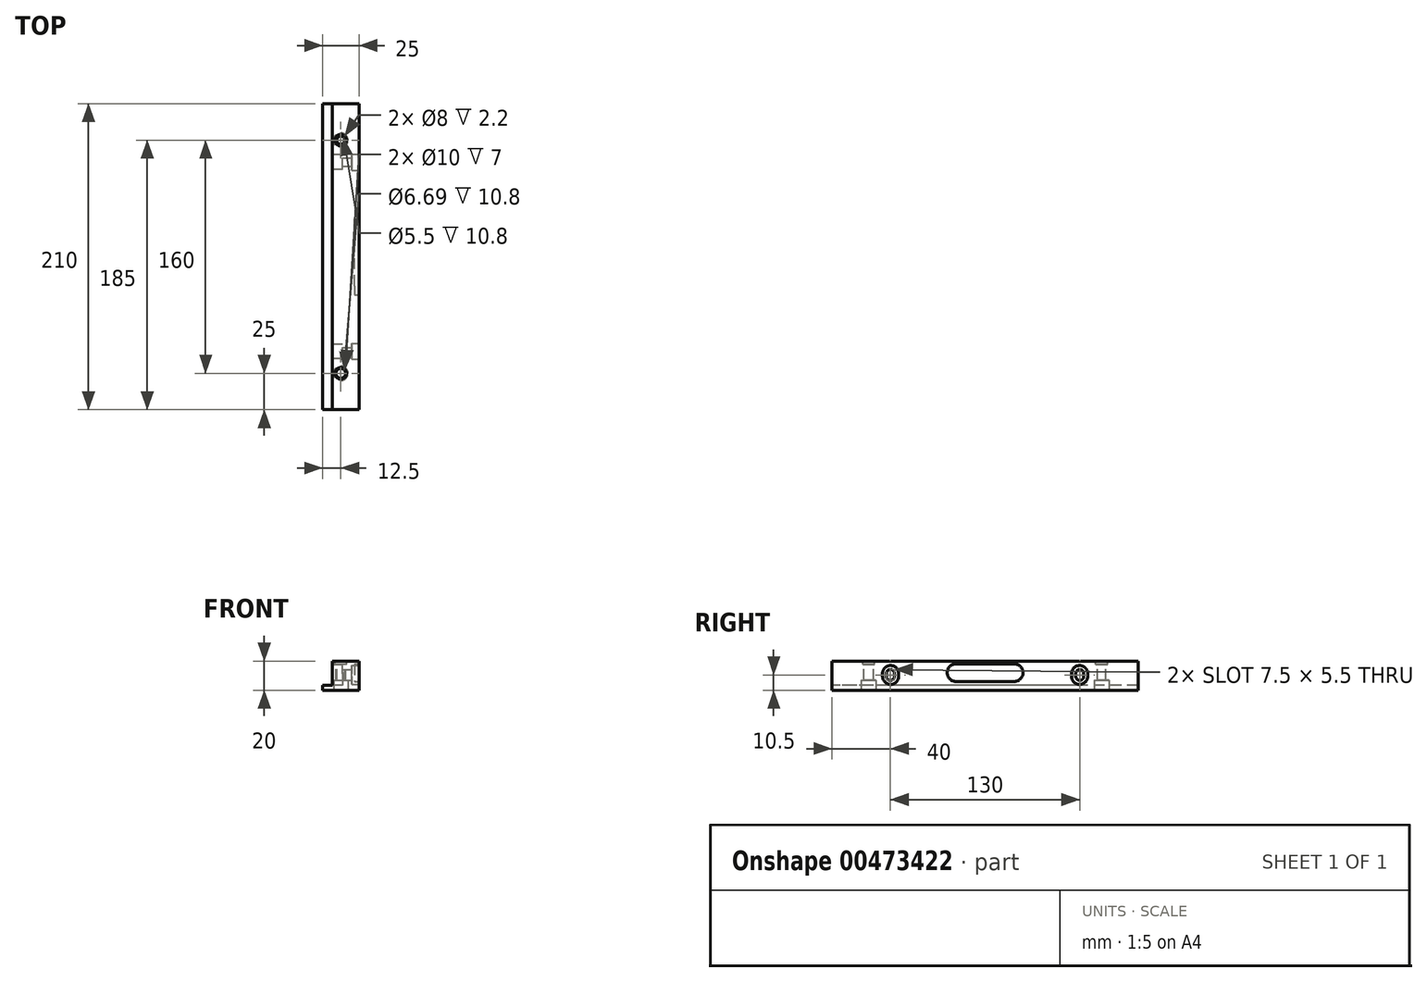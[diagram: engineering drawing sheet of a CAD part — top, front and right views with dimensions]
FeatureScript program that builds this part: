
annotation { "Feature Type Name" : "Feature", "Feature Type Description" : "" }
export const myFeature = defineFeature(function(context is Context, id is Id, definition is map)
    precondition{}
    {
        {
            var Q0;
            Q0=qCreatedBy(makeId("Front.planeOp"),FACE);
            var sketch = newSketch(context, id + "F0", { "sketchPlane" : qUnion([Q0])});
            skLineSegment(sketch, "E0", {"start": v(-12.5, -10) * mm, "end": v(12.5, -10) * mm});
            skLineSegment(sketch, "E1", {"start": v(12.5, 10) * mm, "end": v(-5.7, 10) * mm});
            skLineSegment(sketch, "E2", {"start": v(-5.7, 10) * mm, "end": v(-5.7, -6.5) * mm});
            skLineSegment(sketch, "E3", {"start": v(-5.7, -6.5) * mm, "end": v(-12.5, -6.5) * mm});
            skLineSegment(sketch, "E4", {"start": v(-12.5, -6.5) * mm, "end": v(-12.5, -10) * mm});
            skLineSegment(sketch, "E5", {"start": v(12.5, 10) * mm, "end": v(12.5, -10) * mm});
            skSolve(sketch);
        }
        {
            var Q0;
            Q0 = qSketchRegion(id + "F0", true);
            extrude(context, id + "F1", {"entities" : qUnion([Q0]), "endBound" : BoundingType.SYMMETRIC, "oppositeDirection" : true, "depth" : 210 * mm});
        }
        {
            var Q0;
            Q0=makeQuery(id+"F1.opExtrude","SWEPT_FACE",FACE,{"disambiguationData":[OSD([sQuery(id+"F0.wireOp",EDGE,"E1")])]});
            var sketch = newSketch(context, id + "F2", { "sketchPlane" : qUnion([Q0])});
            skCircle(sketch, "E6", {"center": v(0, 80) * mm, "radius": 2.75 * mm});
            skCircle(sketch, "E7", {"center": v(0, -80) * mm, "radius": 3.34 * mm});
            skSolve(sketch);
        }
        {
            var Q0;
            Q0 = qSketchRegion(id + "F2", true);
            extrude(context, id + "F3", {"entities" : qUnion([Q0]), "operationType" : NewBodyOperationType.REMOVE, "endBound" : BoundingType.THROUGH_ALL, "oppositeDirection" : true, "depth" : 25 * mm});
        }
        {
            var Q0;
            Q0=makeQuery(id+"F1.opExtrude","SWEPT_FACE",FACE,{"disambiguationData":[OSD([sQuery(id+"F0.wireOp",EDGE,"E5")])]});
            var sketch = newSketch(context, id + "F4", { "sketchPlane" : qUnion([Q0])});
            skLineSegment(sketch, "E8.bottom", {"start": v(-65, 4.25) * mm, "end": v(-65, 4.25) * mm});
            skLineSegment(sketch, "E8.top", {"start": v(-65, -3.25) * mm, "end": v(-65, -3.25) * mm});
            skLineSegment(sketch, "E8.left", {"start": v(-67.75, 1.5) * mm, "end": v(-67.75, -0.5) * mm});
            skLineSegment(sketch, "E8.right", {"start": v(-62.25, 1.5) * mm, "end": v(-62.25, -0.5) * mm});
            skLineSegment(sketch, "E9", {"start": v(0, 18.17) * mm, "end": v(0, -22.43) * mm, "construction": true});
            skPoint(sketch, "E9.endSnap0", {"position": v(0, -10) * mm});
            skPoint(sketch, "E10.visualSharp", {"position": v(-67.75, 4.25) * mm});
            skArc(sketch, "E10.filletArc", {"start": v(-65, 4.25) * mm, "mid": v(-66.94, 3.44) * mm, "end": v(-67.75, 1.5) * mm});
            skPoint(sketch, "E11.visualSharp", {"position": v(-62.25, -3.25) * mm});
            skArc(sketch, "E11.filletArc", {"start": v(-65, -3.25) * mm, "mid": v(-63.06, -2.44) * mm, "end": v(-62.25, -0.5) * mm});
            skPoint(sketch, "E12.visualSharp", {"position": v(-62.25, 4.25) * mm});
            skArc(sketch, "E12.filletArc", {"start": v(-62.25, 1.5) * mm, "mid": v(-63.06, 3.44) * mm, "end": v(-65, 4.25) * mm});
            skPoint(sketch, "E13.visualSharp", {"position": v(-67.75, -3.25) * mm});
            skArc(sketch, "E13.filletArc", {"start": v(-67.75, -0.5) * mm, "mid": v(-66.94, -2.44) * mm, "end": v(-65, -3.25) * mm});
            skLineSegment(sketch, "E14.MirrorCS", {"start": v(62.25, 1.5) * mm, "end": v(62.25, -0.5) * mm});
            skLineSegment(sketch, "E15.MirrorCS", {"start": v(67.75, 1.5) * mm, "end": v(67.75, -0.5) * mm});
            skPoint(sketch, "E16.MirrorP", {"position": v(62.25, -3.25) * mm});
            skArc(sketch, "E17.MirrorCS", {"start": v(65, 4.25) * mm, "mid": v(66.94, 3.44) * mm, "end": v(67.75, 1.5) * mm});
            skPoint(sketch, "E18.MirrorP", {"position": v(67.75, -3.25) * mm});
            skPoint(sketch, "E19.MirrorP", {"position": v(62.25, 4.25) * mm});
            skLineSegment(sketch, "E20.MirrorCS", {"start": v(65, 4.25) * mm, "end": v(65, 4.25) * mm});
            skArc(sketch, "E21.MirrorCS", {"start": v(62.25, 1.5) * mm, "mid": v(63.06, 3.44) * mm, "end": v(65, 4.25) * mm});
            skPoint(sketch, "E22.MirrorP", {"position": v(67.75, 4.25) * mm});
            skArc(sketch, "E23.MirrorCS", {"start": v(67.75, -0.5) * mm, "mid": v(66.94, -2.44) * mm, "end": v(65, -3.25) * mm});
            skLineSegment(sketch, "E24.MirrorCS", {"start": v(65, -3.25) * mm, "end": v(65, -3.25) * mm});
            skArc(sketch, "E25.MirrorCS", {"start": v(65, -3.25) * mm, "mid": v(63.06, -2.44) * mm, "end": v(62.25, -0.5) * mm});
            skSolve(sketch);
        }
        {
            var Q0;
            Q0 = qSketchRegion(id + "F4", true);
            extrude(context, id + "F5", {"entities" : qUnion([Q0]), "operationType" : NewBodyOperationType.REMOVE, "endBound" : BoundingType.THROUGH_ALL, "oppositeDirection" : true, "depth" : 25 * mm});
        }
        {
            var Q0;
            Q0=makeQuery(id+"F1.opExtrude","SWEPT_FACE",FACE,{"disambiguationData":[OSD([sQuery(id+"F0.wireOp",EDGE,"E5")])]});
            var sketch = newSketch(context, id + "F6", { "sketchPlane" : qUnion([Q0])});
            skLineSegment(sketch, "E26.bottom", {"start": v(-64.83, -6) * mm, "end": v(-64.86, -6) * mm});
            skLineSegment(sketch, "E26.top", {"start": v(-64.88, 7) * mm, "end": v(-64.9, 7) * mm});
            skLineSegment(sketch, "E26.left", {"start": v(-59.34, -0.38) * mm, "end": v(-59.38, 1.62) * mm});
            skLineSegment(sketch, "E26.right", {"start": v(-70.36, -0.62) * mm, "end": v(-70.5, 5.7) * mm});
            skPoint(sketch, "E26.middle", {"position": v(-64.87, 0.5) * mm});
            skPoint(sketch, "E26.cornerSnap0", {"position": v(-65, -3.25) * mm});
            skPoint(sketch, "E27.visualSharp", {"position": v(-70.24, -6) * mm});
            skArc(sketch, "E27.filletArc", {"start": v(-70.36, -0.62) * mm, "mid": v(-68.7, -4.43) * mm, "end": v(-64.86, -6) * mm});
            skLineSegment(sketch, "E28", {"start": v(-70.4, 1.38) * mm, "end": v(-70.5, 5.7) * mm});
            skPoint(sketch, "E29.visualSharp", {"position": v(-70.53, 7) * mm});
            skArc(sketch, "E29.filletArc", {"start": v(-64.9, 7) * mm, "mid": v(-68.84, 5.35) * mm, "end": v(-70.4, 1.38) * mm});
            skPoint(sketch, "E30.visualSharp", {"position": v(-59.5, 7) * mm});
            skArc(sketch, "E30.filletArc", {"start": v(-59.38, 1.62) * mm, "mid": v(-61.03, 5.43) * mm, "end": v(-64.88, 7) * mm});
            skPoint(sketch, "E31.visualSharp", {"position": v(-59.21, -6) * mm});
            skArc(sketch, "E31.filletArc", {"start": v(-64.83, -6) * mm, "mid": v(-60.9, -4.35) * mm, "end": v(-59.34, -0.38) * mm});
            skLineSegment(sketch, "E32", {"start": v(0, 18.83) * mm, "end": v(0, -21.12) * mm, "construction": true});
            skPoint(sketch, "E32.startSnap0", {"position": v(0, 10) * mm});
            skPoint(sketch, "E32.endSnap0", {"position": v(0, -10) * mm});
            skLineSegment(sketch, "E33.MirrorCS", {"start": v(59.34, -0.38) * mm, "end": v(59.38, 1.62) * mm});
            skLineSegment(sketch, "E34.MirrorCS", {"start": v(70.4, 1.38) * mm, "end": v(70.5, 5.7) * mm});
            skLineSegment(sketch, "E35.MirrorCS", {"start": v(64.83, -6) * mm, "end": v(64.86, -6) * mm});
            skArc(sketch, "E36.MirrorCS", {"start": v(64.83, -6) * mm, "mid": v(60.9, -4.35) * mm, "end": v(59.34, -0.38) * mm});
            skPoint(sketch, "E37.MirrorP", {"position": v(64.87, 0.5) * mm});
            skLineSegment(sketch, "E38.MirrorCS", {"start": v(64.88, 7) * mm, "end": v(64.9, 7) * mm});
            skPoint(sketch, "E39.MirrorP", {"position": v(59.5, 7) * mm});
            skArc(sketch, "E40.MirrorCS", {"start": v(70.36, -0.62) * mm, "mid": v(68.7, -4.43) * mm, "end": v(64.86, -6) * mm});
            skPoint(sketch, "E41.MirrorP", {"position": v(70.53, 7) * mm});
            skPoint(sketch, "E42.MirrorP", {"position": v(59.21, -6) * mm});
            skPoint(sketch, "E43.MirrorP", {"position": v(70.24, -6) * mm});
            skArc(sketch, "E44.MirrorCS", {"start": v(64.9, 7) * mm, "mid": v(68.84, 5.35) * mm, "end": v(70.4, 1.38) * mm});
            skLineSegment(sketch, "E45.MirrorCS", {"start": v(70.36, -0.62) * mm, "end": v(70.5, 5.7) * mm});
            skPoint(sketch, "E46.MirrorP", {"position": v(65, -3.25) * mm});
            skArc(sketch, "E47.MirrorCS", {"start": v(59.38, 1.62) * mm, "mid": v(61.03, 5.43) * mm, "end": v(64.88, 7) * mm});
            skSolve(sketch);
        }
        {
            var Q0;
            Q0 = qSketchRegion(id + "F6", true);
            extrude(context, id + "F7", {"entities" : qUnion([Q0]), "operationType" : NewBodyOperationType.REMOVE, "oppositeDirection" : true, "depth" : 5 * mm});
        }
        {
            var Q0;
            Q0=makeQuery(id+"F1.opExtrude","SWEPT_FACE",FACE,{"disambiguationData":[OSD([sQuery(id+"F0.wireOp",EDGE,"E2")])]});
            var sketch = newSketch(context, id + "F8", { "sketchPlane" : qUnion([Q0])});
            skLineSegment(sketch, "E48", {"start": v(0, 16.2) * mm, "end": v(0, -17.52) * mm, "construction": true});
            skPoint(sketch, "E48.endSnap0", {"position": v(0, 10) * mm});
            skLineSegment(sketch, "E49.bottom", {"start": v(-62.95, 6.83) * mm, "end": v(-62.95, 6.83) * mm});
            skLineSegment(sketch, "E49.top", {"start": v(-65, -6.5) * mm, "end": v(-65, -6.5) * mm});
            skLineSegment(sketch, "E49.left", {"start": v(-70, 2.27) * mm, "end": v(-70, -1.5) * mm});
            skLineSegment(sketch, "E49.right", {"start": v(-60, 2.27) * mm, "end": v(-60, -1.5) * mm});
            skPoint(sketch, "E50.visualSharp", {"position": v(-70, 10) * mm});
            skArc(sketch, "E50.filletArc", {"start": v(-62.95, 6.83) * mm, "mid": v(-67.71, 6.47) * mm, "end": v(-70, 2.27) * mm});
            skPoint(sketch, "E51.visualSharp", {"position": v(-60, 5.5) * mm});
            skArc(sketch, "E51.filletArc", {"start": v(-60, 2.27) * mm, "mid": v(-60.8, 4.98) * mm, "end": v(-62.95, 6.83) * mm});
            skPoint(sketch, "E52.visualSharp", {"position": v(-70, -6.5) * mm});
            skArc(sketch, "E52.filletArc", {"start": v(-70, -1.5) * mm, "mid": v(-68.54, -5.04) * mm, "end": v(-65, -6.5) * mm});
            skPoint(sketch, "E53.visualSharp", {"position": v(-60, -6.5) * mm});
            skArc(sketch, "E53.filletArc", {"start": v(-65, -6.5) * mm, "mid": v(-61.46, -5.04) * mm, "end": v(-60, -1.5) * mm});
            skLineSegment(sketch, "E54.MirrorCS", {"start": v(70, 2.27) * mm, "end": v(70, -1.5) * mm});
            skLineSegment(sketch, "E55.MirrorCS", {"start": v(60, 2.27) * mm, "end": v(60, -1.5) * mm});
            skArc(sketch, "E56.MirrorCS", {"start": v(60, 2.27) * mm, "mid": v(60.8, 4.98) * mm, "end": v(62.95, 6.83) * mm});
            skArc(sketch, "E57.MirrorCS", {"start": v(62.95, 6.83) * mm, "mid": v(67.71, 6.47) * mm, "end": v(70, 2.27) * mm});
            skArc(sketch, "E58.MirrorCS", {"start": v(65, -6.5) * mm, "mid": v(61.46, -5.04) * mm, "end": v(60, -1.5) * mm});
            skArc(sketch, "E59.MirrorCS", {"start": v(70, -1.5) * mm, "mid": v(68.54, -5.04) * mm, "end": v(65, -6.5) * mm});
            skPoint(sketch, "E60.MirrorP", {"position": v(60, -6.5) * mm});
            skLineSegment(sketch, "E61.MirrorCS", {"start": v(62.95, 6.83) * mm, "end": v(62.95, 6.83) * mm});
            skPoint(sketch, "E62.MirrorP", {"position": v(70, 10) * mm});
            skPoint(sketch, "E63.MirrorP", {"position": v(60, 5.5) * mm});
            skPoint(sketch, "E64.MirrorP", {"position": v(70, -6.5) * mm});
            skLineSegment(sketch, "E65.MirrorCS", {"start": v(65, -6.5) * mm, "end": v(65, -6.5) * mm});
            skSolve(sketch);
        }
        {
            var Q0;
            {var subQ0=makeQuery(id+"F1.opExtrude","SWEPT_FACE",FACE,{"disambiguationData":[OSD([sQuery(id+"F0.wireOp",EDGE,"E2")])]});Q0=makeQuery(id+"F8.imprint","IMPRINT",FACE,{"disambiguationData":[TD([[makeQuery(id+"F8.imprint","IMPRINT",EDGE,{"derivedFrom":makeQuery(id+"F5.boolean.opBoolean","INTERSECT",EDGE,{"derivedFrom":[subQ0,makeQuery(id+"F5.opExtrude","SWEPT_FACE",FACE,{"disambiguationData":[OSD([sQuery(id+"F4.wireOp",EDGE,"E8.left")])]})]})}),1.0]])]});}
            var Q1;
            {var subQ0=makeQuery(id+"F1.opExtrude","SWEPT_FACE",FACE,{"disambiguationData":[OSD([sQuery(id+"F0.wireOp",EDGE,"E2")])]});Q1=makeQuery(id+"F8.imprint","IMPRINT",FACE,{"disambiguationData":[TD([[makeQuery(id+"F8.imprint","IMPRINT",EDGE,{"derivedFrom":makeQuery(id+"F5.boolean.opBoolean","INTERSECT",EDGE,{"derivedFrom":[subQ0,makeQuery(id+"F5.opExtrude","SWEPT_FACE",FACE,{"disambiguationData":[OSD([sQuery(id+"F4.wireOp",EDGE,"E14.MirrorCS")])]})]})}),1.0]])]});}
            var Q2;
            Q2=makeQuery(id+"F8.imprint","IMPRINT",FACE,{"disambiguationData":[TD([[makeQuery(id+"F8.imprint","IMPRINT",EDGE,{"derivedFrom":sQuery(id+"F8.wireOp",EDGE,"E49.left")}),1.0]])]});
            var Q3;
            Q3=makeQuery(id+"F8.imprint","IMPRINT",FACE,{"disambiguationData":[TD([[makeQuery(id+"F8.imprint","IMPRINT",EDGE,{"derivedFrom":sQuery(id+"F8.wireOp",EDGE,"E54.MirrorCS")}),-1.0]])]});
            extrude(context, id + "F9", {"entities" : qUnion([Q0, Q1, Q2, Q3]), "operationType" : NewBodyOperationType.REMOVE, "oppositeDirection" : true, "depth" : 7 * mm});
        }
        {
            var Q0;
            Q0=makeQuery(id+"F1.opExtrude","SWEPT_FACE",FACE,{"disambiguationData":[OSD([sQuery(id+"F0.wireOp",EDGE,"E1")])]});
            var sketch = newSketch(context, id + "F10", { "sketchPlane" : qUnion([Q0])});
            skLineSegment(sketch, "E66", {"start": v(26.36, 0) * mm, "end": v(-24.98, 0) * mm, "construction": true});
            skPoint(sketch, "E66.startSnap0", {"position": v(12.5, 0) * mm});
            skPoint(sketch, "E66.endSnap0", {"position": v(-5.7, 0) * mm});
            skCircle(sketch, "E67", {"center": v(0, -80) * mm, "radius": 4 * mm});
            skCircle(sketch, "E68.MirrorC", {"center": v(0, 80) * mm, "radius": 4 * mm});
            skSolve(sketch);
        }
        {
            var Q0;
            Q0 = qSketchRegion(id + "F10", true);
            extrude(context, id + "F11", {"entities" : qUnion([Q0]), "operationType" : NewBodyOperationType.REMOVE, "oppositeDirection" : true, "depth" : 2.2 * mm});
        }
        {
            var Q0;
            Q0=makeQuery(id+"F1.opExtrude","SWEPT_FACE",FACE,{"disambiguationData":[OSD([sQuery(id+"F0.wireOp",EDGE,"E0")])]});
            var sketch = newSketch(context, id + "F12", { "sketchPlane" : qUnion([Q0])});
            skCircle(sketch, "E69", {"center": v(0, 80) * mm, "radius": 5 * mm});
            skLineSegment(sketch, "E70", {"start": v(-22.23, 0) * mm, "end": v(27.73, 0) * mm, "construction": true});
            skPoint(sketch, "E70.endSnap0", {"position": v(12.5, 0) * mm});
            skCircle(sketch, "E71.MirrorC", {"center": v(0, -80) * mm, "radius": 5 * mm});
            skSolve(sketch);
        }
        {
            var Q0;
            Q0 = qSketchRegion(id + "F12", true);
            extrude(context, id + "F13", {"entities" : qUnion([Q0]), "operationType" : NewBodyOperationType.REMOVE, "oppositeDirection" : true, "depth" : 7 * mm});
        }
        {
            var Q0;
            Q0=makeQuery(id+"F1.opExtrude","SWEPT_FACE",FACE,{"disambiguationData":[OSD([sQuery(id+"F0.wireOp",EDGE,"E5")])]});
            var sketch = newSketch(context, id + "F14", { "sketchPlane" : qUnion([Q0])});
            skLineSegment(sketch, "E72.bottom", {"start": v(-20, 8) * mm, "end": v(20, 8) * mm});
            skLineSegment(sketch, "E72.top", {"start": v(-20, -4) * mm, "end": v(20, -4) * mm});
            skLineSegment(sketch, "E72.left", {"start": v(-26, 2) * mm, "end": v(-26, 2) * mm});
            skLineSegment(sketch, "E72.right", {"start": v(26, 2) * mm, "end": v(26, 2) * mm});
            skPoint(sketch, "E73.visualSharp", {"position": v(-26, 8) * mm});
            skArc(sketch, "E73.filletArc", {"start": v(-20, 8) * mm, "mid": v(-24.24, 6.24) * mm, "end": v(-26, 2) * mm});
            skPoint(sketch, "E74.visualSharp", {"position": v(-26, -4) * mm});
            skArc(sketch, "E74.filletArc", {"start": v(-26, 2) * mm, "mid": v(-24.24, -2.24) * mm, "end": v(-20, -4) * mm});
            skPoint(sketch, "E75.visualSharp", {"position": v(26, 8) * mm});
            skArc(sketch, "E75.filletArc", {"start": v(26, 2) * mm, "mid": v(24.24, 6.24) * mm, "end": v(20, 8) * mm});
            skPoint(sketch, "E76.visualSharp", {"position": v(26, -4) * mm});
            skArc(sketch, "E76.filletArc", {"start": v(20, -4) * mm, "mid": v(24.24, -2.24) * mm, "end": v(26, 2) * mm});
            skSolve(sketch);
        }
        {
            var Q0;
            Q0 = qSketchRegion(id + "F14", true);
            extrude(context, id + "F15", {"entities" : qUnion([Q0]), "operationType" : NewBodyOperationType.REMOVE, "oppositeDirection" : true, "depth" : 3 * mm});
        }
    });
